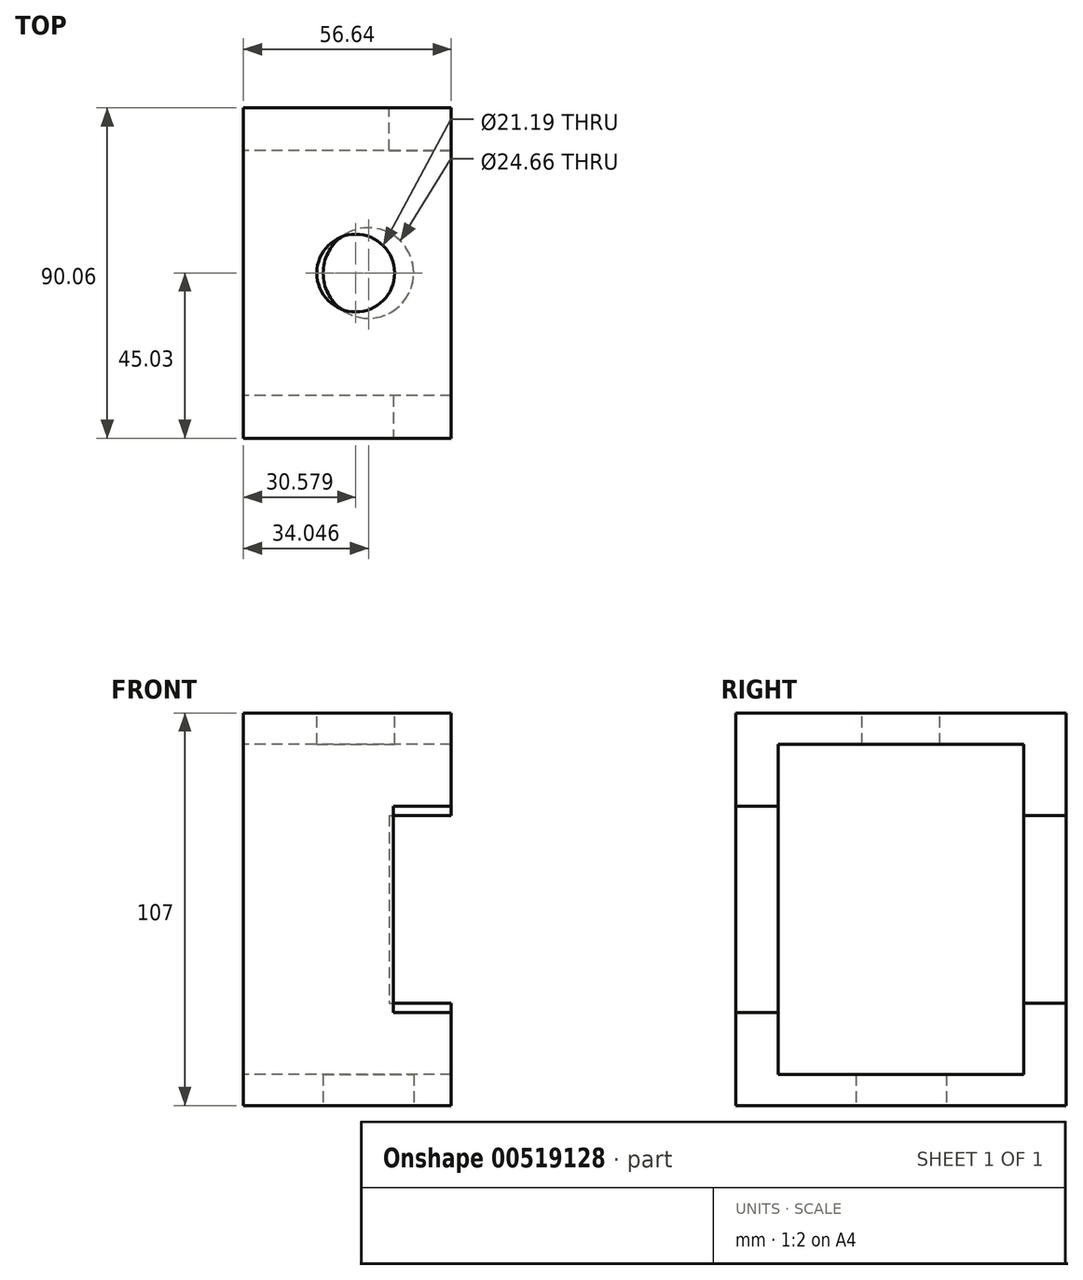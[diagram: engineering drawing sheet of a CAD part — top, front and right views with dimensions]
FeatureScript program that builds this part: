
annotation { "Feature Type Name" : "Feature", "Feature Type Description" : "" }
export const myFeature = defineFeature(function(context is Context, id is Id, definition is map)
    precondition{}
    {
        {
            var Q0;
            Q0=qCreatedBy(makeId("Right.planeOp"),FACE);
            var sketch = newSketch(context, id + "F0", { "sketchPlane" : qUnion([Q0])});
            skLineSegment(sketch, "E0.bottom", {"start": v(45.03, 53.5) * mm, "end": v(-45.03, 53.5) * mm});
            skLineSegment(sketch, "E0.top", {"start": v(45.03, -53.5) * mm, "end": v(-45.03, -53.5) * mm});
            skLineSegment(sketch, "E0.left", {"start": v(45.03, 53.5) * mm, "end": v(45.03, -53.5) * mm});
            skLineSegment(sketch, "E0.right", {"start": v(-45.03, 53.5) * mm, "end": v(-45.03, -53.5) * mm});
            skPoint(sketch, "E0.middle", {"position": v(0, 0) * mm});
            skLineSegment(sketch, "E1.bottom", {"start": v(33.44, 45.03) * mm, "end": v(-33.44, 45.03) * mm});
            skLineSegment(sketch, "E1.top", {"start": v(33.44, -45.03) * mm, "end": v(-33.44, -45.03) * mm});
            skLineSegment(sketch, "E1.left", {"start": v(33.44, 45.03) * mm, "end": v(33.44, -45.03) * mm});
            skLineSegment(sketch, "E1.right", {"start": v(-33.44, 45.03) * mm, "end": v(-33.44, -45.03) * mm});
            skSolve(sketch);
        }
        {
            var Q0;
            Q0=makeQuery(id+"F0.imprint","IMPRINT",FACE,{"disambiguationData":[TD([[makeQuery(id+"F0.imprint","IMPRINT",EDGE,{"derivedFrom":sQuery(id+"F0.wireOp",EDGE,"E0.bottom")}),1.0]])]});
            extrude(context, id + "F1", {"entities" : qUnion([Q0]), "depth" : 56.64 * mm, "offsetDistance" : 25.4 * mm});
        }
        {
            var Q0;
            Q0=makeQuery(id+"F1.opExtrude","SWEPT_FACE",FACE,{"disambiguationData":[OSD([sQuery(id+"F0.wireOp",EDGE,"E0.left")])]});
            var sketch = newSketch(context, id + "F2", { "sketchPlane" : qUnion([Q0])});
            skLineSegment(sketch, "E2.bottom", {"start": v(-39.74, 25.6) * mm, "end": v(-73.55, 25.6) * mm});
            skLineSegment(sketch, "E2.top", {"start": v(-39.74, -25.6) * mm, "end": v(-73.55, -25.6) * mm});
            skLineSegment(sketch, "E2.left", {"start": v(-39.74, 25.6) * mm, "end": v(-39.74, -25.6) * mm});
            skLineSegment(sketch, "E2.right", {"start": v(-73.55, 25.6) * mm, "end": v(-73.55, -25.6) * mm});
            skPoint(sketch, "E2.middle", {"position": v(-56.64, 0) * mm});
            skSolve(sketch);
        }
        {
            var Q0;
            {var subQ0=sQuery(id+"F2.wireOp",EDGE,"E2.left");Q0=makeQuery(id+"F2.imprint","IMPRINT",FACE,{"disambiguationData":[TD([[makeQuery(id+"F2.imprint","IMPRINT",EDGE,{"derivedFrom":subQ0}),-1.0]])]});}
            extrude(context, id + "F3", {"entities" : qUnion([Q0]), "operationType" : NewBodyOperationType.REMOVE, "oppositeDirection" : true, "depth" : 25.4 * mm, "offsetDistance" : 25.4 * mm});
        }
        {
            var Q0;
            Q0=makeQuery(id+"F1.opExtrude","SWEPT_FACE",FACE,{"disambiguationData":[OSD([sQuery(id+"F0.wireOp",EDGE,"E0.right")])]});
            var sketch = newSketch(context, id + "F4", { "sketchPlane" : qUnion([Q0])});
            skLineSegment(sketch, "E3.bottom", {"start": v(40.86, -28.09) * mm, "end": v(72.42, -28.09) * mm});
            skLineSegment(sketch, "E3.top", {"start": v(40.86, 28.09) * mm, "end": v(72.42, 28.09) * mm});
            skLineSegment(sketch, "E3.left", {"start": v(40.86, -28.09) * mm, "end": v(40.86, 28.09) * mm});
            skLineSegment(sketch, "E3.right", {"start": v(72.42, -28.09) * mm, "end": v(72.42, 28.09) * mm});
            skPoint(sketch, "E3.middle", {"position": v(56.64, 0) * mm});
            skSolve(sketch);
        }
        {
            var Q0;
            {var subQ0=sQuery(id+"F4.wireOp",EDGE,"E3.left");Q0=makeQuery(id+"F4.imprint","IMPRINT",FACE,{"disambiguationData":[TD([[makeQuery(id+"F4.imprint","IMPRINT",EDGE,{"derivedFrom":subQ0}),-1.0]])]});}
            extrude(context, id + "F5", {"entities" : qUnion([Q0]), "operationType" : NewBodyOperationType.REMOVE, "oppositeDirection" : true, "depth" : 25.4 * mm, "offsetDistance" : 25.4 * mm});
        }
        {
            var Q0;
            Q0=makeQuery(id+"F1.opExtrude","SWEPT_FACE",FACE,{"disambiguationData":[OSD([sQuery(id+"F0.wireOp",EDGE,"E0.bottom")])]});
            var sketch = newSketch(context, id + "F6", { "sketchPlane" : qUnion([Q0])});
            skCircle(sketch, "E4", {"center": v(30.58, 0) * mm, "radius": 10.6 * mm});
            skSolve(sketch);
        }
        {
            var Q0;
            Q0=makeQuery(id+"F6.imprint","IMPRINT",FACE,{"disambiguationData":[TD([[makeQuery(id+"F6.imprint","IMPRINT",EDGE,{"derivedFrom":sQuery(id+"F6.wireOp",EDGE,"E4")}),1.0]])]});
            extrude(context, id + "F7", {"entities" : qUnion([Q0]), "operationType" : NewBodyOperationType.REMOVE, "oppositeDirection" : true, "depth" : 25.4 * mm, "offsetDistance" : 25.4 * mm});
        }
        {
            var Q0;
            Q0=makeQuery(id+"F1.opExtrude","SWEPT_FACE",FACE,{"disambiguationData":[OSD([sQuery(id+"F0.wireOp",EDGE,"E0.top")])]});
            var sketch = newSketch(context, id + "F8", { "sketchPlane" : qUnion([Q0])});
            skCircle(sketch, "E5", {"center": v(34.05, 0) * mm, "radius": 12.33 * mm});
            skSolve(sketch);
        }
        {
            var Q0;
            Q0=makeQuery(id+"F8.imprint","IMPRINT",FACE,{"disambiguationData":[TD([[makeQuery(id+"F8.imprint","IMPRINT",EDGE,{"derivedFrom":sQuery(id+"F8.wireOp",EDGE,"E5")}),1.0]])]});
            extrude(context, id + "F9", {"entities" : qUnion([Q0]), "operationType" : NewBodyOperationType.REMOVE, "oppositeDirection" : true, "depth" : 25.4 * mm, "offsetDistance" : 25.4 * mm});
        }
    });
